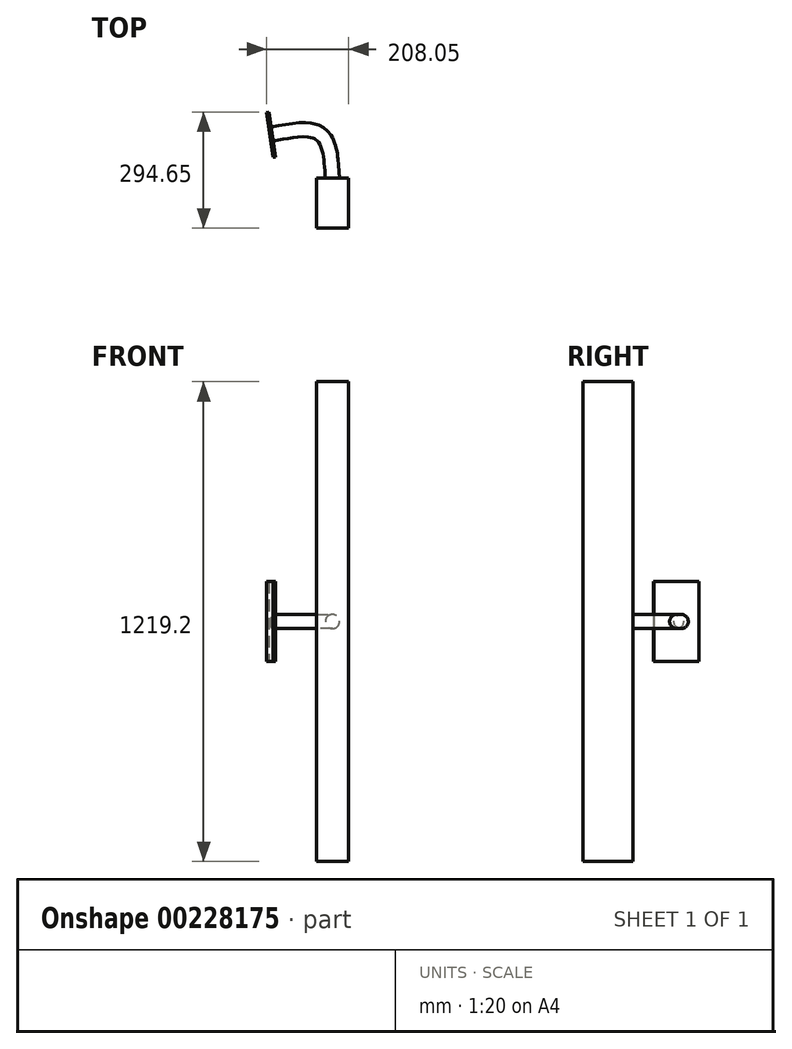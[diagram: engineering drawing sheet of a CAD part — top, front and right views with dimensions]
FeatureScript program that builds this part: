
annotation { "Feature Type Name" : "Feature", "Feature Type Description" : "" }
export const myFeature = defineFeature(function(context is Context, id is Id, definition is map)
    precondition{}
    {
        {
            var Q0;
            Q0=qCreatedBy(makeId("Front.planeOp"),FACE);
            var sketch = newSketch(context, id + "F0", { "sketchPlane" : qUnion([Q0])});
            skLineSegment(sketch, "E0.bottom", {"start": v(-41.02, 609.6) * mm, "end": v(41.02, 609.6) * mm});
            skLineSegment(sketch, "E0.top", {"start": v(-41.02, -609.6) * mm, "end": v(41.02, -609.6) * mm});
            skLineSegment(sketch, "E0.left", {"start": v(-41.02, 609.6) * mm, "end": v(-41.02, -609.6) * mm});
            skLineSegment(sketch, "E0.right", {"start": v(41.02, 609.6) * mm, "end": v(41.02, -609.6) * mm});
            skPoint(sketch, "E0.middle", {"position": v(0, 0) * mm});
            skSolve(sketch);
        }
        {
            var Q0;
            Q0=makeQuery(id+"F0.imprint","IMPRINT",FACE,{"disambiguationData":[TD([[makeQuery(id+"F0.imprint","IMPRINT",EDGE,{"derivedFrom":sQuery(id+"F0.wireOp",EDGE,"E0.bottom")}),-1.0]])]});
            extrude(context, id + "F1", {"entities" : qUnion([Q0]), "depth" : 127 * mm});
        }
        {
            var Q0;
            Q0=qCreatedBy(makeId("Top.planeOp"),FACE);
            var sketch = newSketch(context, id + "F2", { "sketchPlane" : qUnion([Q0])});
            skLineSegment(sketch, "E1.bottom", {"start": v(-130.62, 28.2) * mm, "end": v(-964.8, -195.31) * mm});
            skLineSegment(sketch, "E1.top", {"start": v(-175.4, 195.31) * mm, "end": v(-1009.57, -28.2) * mm});
            skLineSegment(sketch, "E1.left", {"start": v(-130.62, 28.2) * mm, "end": v(-175.4, 195.31) * mm});
            skLineSegment(sketch, "E1.right", {"start": v(-964.8, -195.31) * mm, "end": v(-1009.57, -28.2) * mm});
            skPoint(sketch, "E1.middle", {"position": v(-570.1, 0) * mm});
            skLineSegment(sketch, "E2", {"start": v(0, 0) * mm, "end": v(156.17, 156.17) * mm});
            skPoint(sketch, "E3.1.internal.snap0", {"position": v(-153.01, 111.76) * mm});
            skFitSpline(sketch, "E3", {"points": [v(-153.01, 111.76) * mm, v(-30.27, 111.76) * mm, v(0, 0) * mm], "startDerivative": vector(287.75, 57.53) * mm, "endDerivative": vector(16.96, -282.7) * mm});
            skSolve(sketch);
        }
        {
            var Q0;
            Q0=qCreatedBy(makeId("Front.planeOp"),FACE);
            var sketch = newSketch(context, id + "F3", { "sketchPlane" : qUnion([Q0])});
            skCircle(sketch, "E4", {"center": v(0, 0) * mm, "radius": 18.07 * mm});
            skSolve(sketch);
        }
        {
            var Q0;
            Q0=makeQuery(id+"F3.imprint","IMPRINT",FACE,{"disambiguationData":[TD([[makeQuery(id+"F3.imprint","IMPRINT",EDGE,{"derivedFrom":sQuery(id+"F3.wireOp",EDGE,"E4")}),1.0]])]});
            var Q1;
            Q1=sQuery(id+"F2.wireOp",EDGE,"E3");
            sweep(context, id + "F4", {"operationType" : NewBodyOperationType.ADD, "profiles" : qUnion([Q0]), "path" : qUnion([Q1])});
        }
        {
            var Q0;
            Q0=qCreatedBy(makeId("Top.planeOp"),FACE);
            var sketch = newSketch(context, id + "F5", { "sketchPlane" : qUnion([Q0])});
            skLineSegment(sketch, "E5.bottom", {"start": v(-167.03, 166.78) * mm, "end": v(-160.74, 167.65) * mm});
            skLineSegment(sketch, "E5.top", {"start": v(-151.3, 53) * mm, "end": v(-145, 53.87) * mm});
            skLineSegment(sketch, "E5.left", {"start": v(-167.03, 166.78) * mm, "end": v(-151.3, 53) * mm});
            skLineSegment(sketch, "E5.right", {"start": v(-160.74, 167.65) * mm, "end": v(-145, 53.87) * mm});
            skPoint(sketch, "E5.middle", {"position": v(-156.02, 110.32) * mm});
            skSolve(sketch);
        }
        {
            var Q0;
            Q0=makeQuery(id+"F5.imprint","IMPRINT",FACE,{"disambiguationData":[TD([[makeQuery(id+"F5.imprint","IMPRINT",EDGE,{"derivedFrom":sQuery(id+"F5.wireOp",EDGE,"E5.bottom")}),-1.0]])]});
            extrude(context, id + "F6", {"entities" : qUnion([Q0]), "operationType" : NewBodyOperationType.ADD, "endBound" : BoundingType.SYMMETRIC, "depth" : 203.2 * mm});
        }
    });
